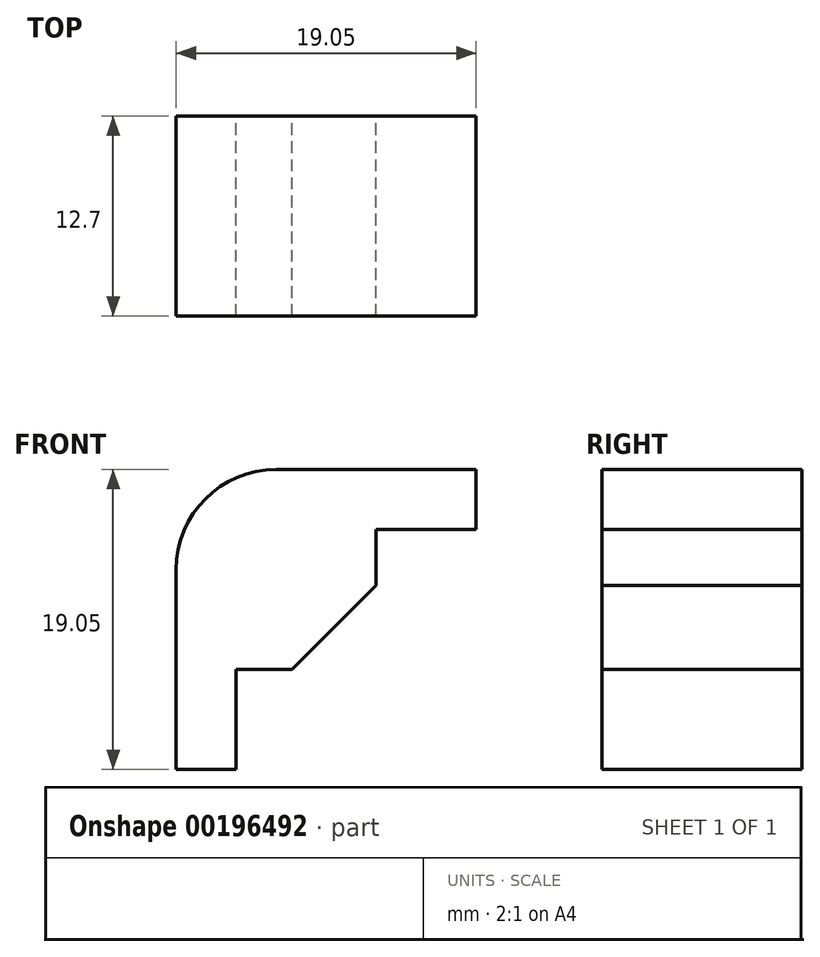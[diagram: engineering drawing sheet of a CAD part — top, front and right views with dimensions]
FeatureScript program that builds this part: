
annotation { "Feature Type Name" : "Feature", "Feature Type Description" : "" }
export const myFeature = defineFeature(function(context is Context, id is Id, definition is map)
    precondition{}
    {
        {
            var Q0;
            Q0=qCreatedBy(makeId("Front.planeOp"),FACE);
            var sketch = newSketch(context, id + "F0", { "sketchPlane" : qUnion([Q0])});
            skLineSegment(sketch, "E0.right", {"start": v(84.3, 21.12) * mm, "end": v(72.84, 24.68) * mm, "construction": true});
            skPoint(sketch, "E0.middle", {"position": v(52.8, 22.9) * mm});
            skLineSegment(sketch, "E1.bottom", {"start": v(11.18, -2.18) * mm, "end": v(17.03, -2.18) * mm, "construction": true});
            skPoint(sketch, "E1.middle", {"position": v(14.1, 6.6) * mm});
            skLineSegment(sketch, "E2", {"start": v(20.07, 24.68) * mm, "end": v(26.42, 24.68) * mm});
            skLineSegment(sketch, "E3", {"start": v(26.42, 24.68) * mm, "end": v(26.42, 28.49) * mm});
            skLineSegment(sketch, "E4", {"start": v(26.42, 28.49) * mm, "end": v(13.72, 28.49) * mm});
            skLineSegment(sketch, "E5", {"start": v(7.37, 22.14) * mm, "end": v(7.37, 9.44) * mm});
            skLineSegment(sketch, "E6", {"start": v(7.37, 9.44) * mm, "end": v(11.18, 9.44) * mm});
            skLineSegment(sketch, "E7", {"start": v(11.18, 9.44) * mm, "end": v(11.18, 15.79) * mm});
            skPoint(sketch, "E8.visualSharp", {"position": v(7.37, 28.49) * mm});
            skArc(sketch, "E8.filletArc", {"start": v(13.72, 28.49) * mm, "mid": v(9.23, 26.63) * mm, "end": v(7.37, 22.14) * mm});
            skLineSegment(sketch, "E9", {"start": v(11.18, 15.79) * mm, "end": v(14.73, 15.79) * mm});
            skLineSegment(sketch, "E10", {"start": v(14.73, 15.79) * mm, "end": v(20.07, 21.12) * mm});
            skLineSegment(sketch, "E11", {"start": v(20.07, 21.12) * mm, "end": v(20.07, 24.68) * mm});
            skPoint(sketch, "E12.end.orphan", {"position": v(32.76, 21.12) * mm});
            skPoint(sketch, "E1.right.end.orphan", {"position": v(17.03, 15.4) * mm});
            skPoint(sketch, "E13.orphan", {"position": v(11.18, 15.4) * mm});
            skLineSegment(sketch, "E14", {"start": v(20.07, 24.68) * mm, "end": v(20.07, 24.68) * mm});
            skPoint(sketch, "E15.orphan", {"position": v(21.3, 24.68) * mm});
            skSolve(sketch);
        }
        {
            var Q0;
            Q0=makeQuery(id+"F0.imprint","IMPRINT",FACE,{"disambiguationData":[TD([[makeQuery(id+"F0.imprint","IMPRINT",EDGE,{"derivedFrom":sQuery(id+"F0.wireOp",EDGE,"E12")}),1.0]])]});
            var Q1;
            Q1=makeQuery(id+"F0.imprint","IMPRINT",FACE,{"disambiguationData":[TD([[makeQuery(id+"F0.imprint","IMPRINT",EDGE,{"derivedFrom":sQuery(id+"F0.wireOp",EDGE,"E2")}),1.0]])]});
            extrude(context, id + "F1", {"entities" : qUnion([Q0, Q1]), "depth" : 12.7 * mm});
        }
    });
